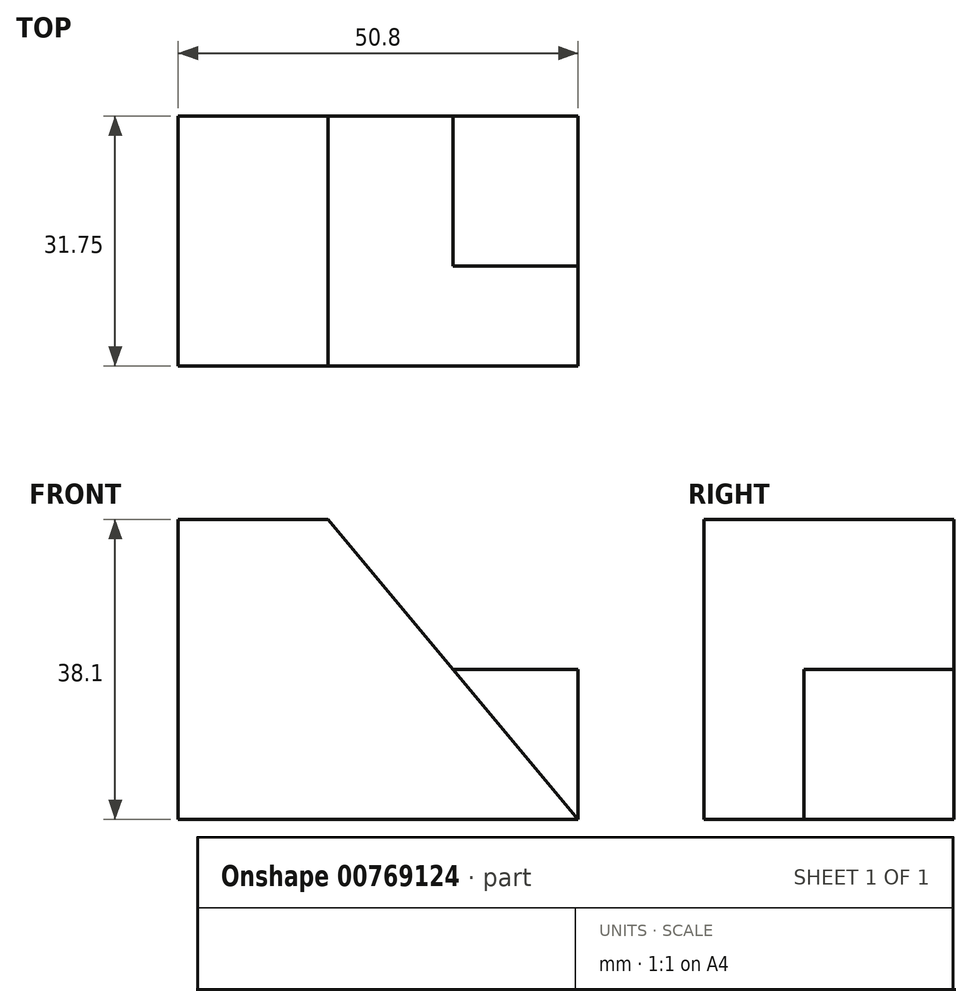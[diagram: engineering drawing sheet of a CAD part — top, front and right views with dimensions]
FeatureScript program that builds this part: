
annotation { "Feature Type Name" : "Feature", "Feature Type Description" : "" }
export const myFeature = defineFeature(function(context is Context, id is Id, definition is map)
    precondition{}
    {
        {
            var Q0;
            Q0=qCreatedBy(makeId("Front.planeOp"),FACE);
            var sketch = newSketch(context, id + "F0", { "sketchPlane" : qUnion([Q0])});
            skLineSegment(sketch, "E0", {"start": v(0, 0) * mm, "end": v(50.8, 0) * mm});
            skLineSegment(sketch, "E1", {"start": v(0, 0) * mm, "end": v(0, 38.1) * mm});
            skLineSegment(sketch, "E2", {"start": v(0, 38.1) * mm, "end": v(19.05, 38.1) * mm});
            skLineSegment(sketch, "E3", {"start": v(19.05, 38.1) * mm, "end": v(50.8, 0) * mm});
            skSolve(sketch);
        }
        {
            var Q0;
            Q0=makeQuery(id+"F0.imprint","IMPRINT",FACE,{"disambiguationData":[TD([[makeQuery(id+"F0.imprint","IMPRINT",EDGE,{"derivedFrom":sQuery(id+"F0.wireOp",EDGE,"E0")}),1.0]])]});
            extrude(context, id + "F1", {"entities" : qUnion([Q0]), "depth" : 31.75 * mm, "offsetDistance" : 25.4 * mm});
        }
        {
            var Q0;
            Q0=makeQuery(id+"F1.opExtrude","CAP_FACE",FACE,{"disambiguationData":[OSD([sQuery(id+"F0.wireOp",EDGE,"E0"),sQuery(id+"F0.wireOp",EDGE,"E1"),sQuery(id+"F0.wireOp",EDGE,"E2"),sQuery(id+"F0.wireOp",EDGE,"E3")])],"isStart":true});
            var sketch = newSketch(context, id + "F2", { "sketchPlane" : qUnion([Q0])});
            skLineSegment(sketch, "E4", {"start": v(-50.8, 0) * mm, "end": v(-50.8, 19.05) * mm});
            skLineSegment(sketch, "E5", {"start": v(-50.8, 19.05) * mm, "end": v(-34.93, 19.05) * mm});
            skLineSegment(sketch, "E6", {"start": v(-34.93, 19.05) * mm, "end": v(-50.8, 0) * mm});
            skSolve(sketch);
        }
        {
            var Q0;
            Q0 = qSketchRegion(id + "F2", true);
            extrude(context, id + "F3", {"entities" : qUnion([Q0]), "operationType" : NewBodyOperationType.ADD, "oppositeDirection" : true, "depth" : 19.05 * mm, "offsetDistance" : 25.4 * mm});
        }
    });
